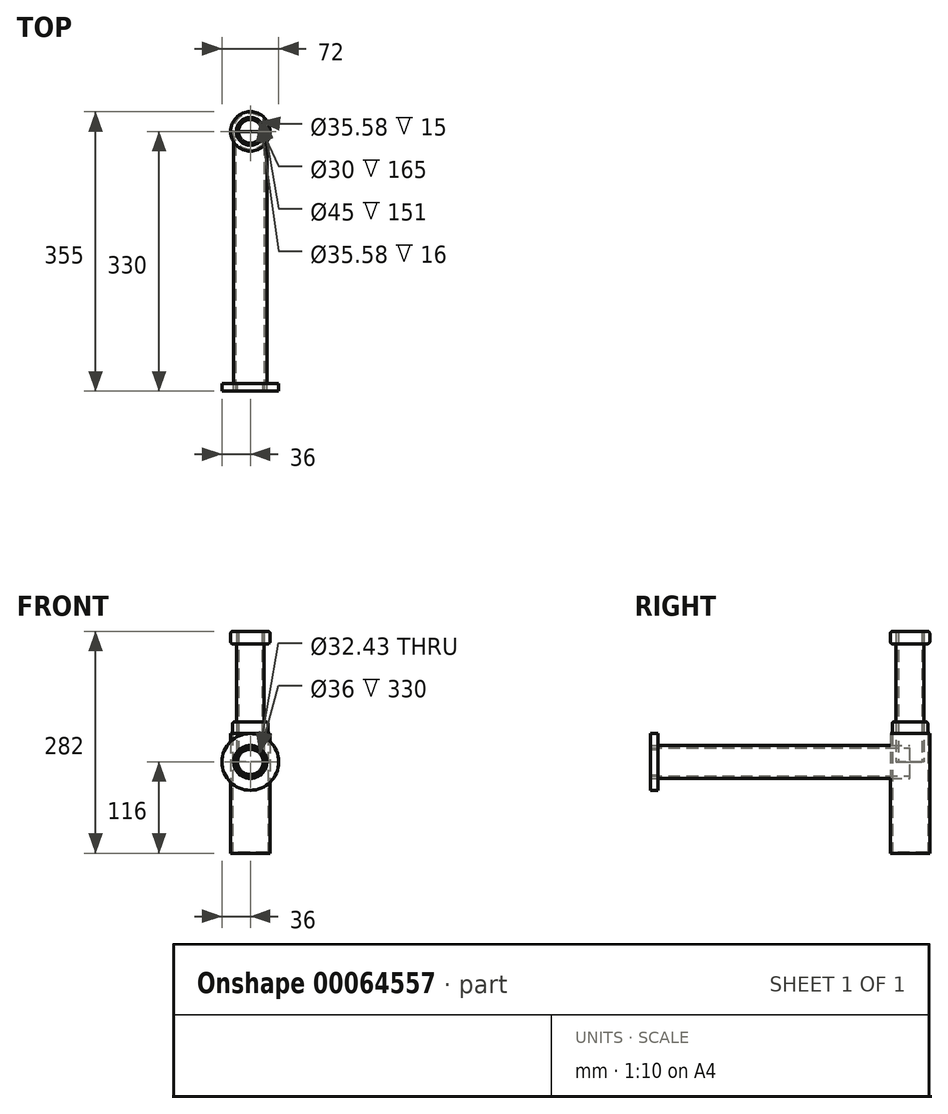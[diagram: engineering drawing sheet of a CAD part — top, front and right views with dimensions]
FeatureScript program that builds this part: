
annotation { "Feature Type Name" : "Feature", "Feature Type Description" : "" }
export const myFeature = defineFeature(function(context is Context, id is Id, definition is map)
    precondition{}
    {
        {
            var Q0;
            Q0=qCreatedBy(makeId("Front.planeOp"),FACE);
            var sketch = newSketch(context, id + "F0", { "sketchPlane" : qUnion([Q0])});
            skCircle(sketch, "E0", {"center": v(0, 0) * mm, "radius": 21 * mm});
            skCircle(sketch, "E1", {"center": v(0, 0) * mm, "radius": 18 * mm});
            skSolve(sketch);
        }
        {
            var Q0;
            Q0=makeQuery(id+"F0.imprint","IMPRINT",FACE,{"disambiguationData":[TD([[makeQuery(id+"F0.imprint","IMPRINT",EDGE,{"derivedFrom":sQuery(id+"F0.wireOp",EDGE,"E0")}),1.0]])]});
            extrude(context, id + "F1", {"entities" : qUnion([Q0]), "depth" : 330 * mm});
        }
        {
            var Q0;
            Q0=qCreatedBy(makeId("Top.planeOp"),FACE);
            var sketch = newSketch(context, id + "F2", { "sketchPlane" : qUnion([Q0])});
            skCircle(sketch, "E2", {"center": v(0, 0) * mm, "radius": 25 * mm});
            skCircle(sketch, "E3", {"center": v(0, 0) * mm, "radius": 22.5 * mm});
            skSolve(sketch);
        }
        {
            var Q0;
            Q0=makeQuery(id+"F2.imprint","IMPRINT",FACE,{"disambiguationData":[TD([[makeQuery(id+"F2.imprint","IMPRINT",EDGE,{"derivedFrom":sQuery(id+"F2.wireOp",EDGE,"E2")}),1.0]])]});
            extrude(context, id + "F3", {"entities" : qUnion([Q0]), "depth" : 36 * mm, "hasSecondDirection" : true, "secondDirectionOppositeDirection" : true, "secondDirectionDepth" : 115 * mm});
        }
        {
            var Q0;
            Q0=makeQuery(id+"F3.opExtrude","CAP_FACE",FACE,{"disambiguationData":[OSD([sQuery(id+"F2.wireOp",EDGE,"E2"),sQuery(id+"F2.wireOp",EDGE,"E3")])],"isStart":false});
            var sketch = newSketch(context, id + "F4", { "sketchPlane" : qUnion([Q0])});
            skCircle(sketch, "E4", {"center": v(0, 0) * mm, "radius": 25 * mm});
            skCircle(sketch, "E5", {"center": v(0, 0) * mm, "radius": 17.79 * mm});
            skSolve(sketch);
        }
        {
            var Q0;
            Q0=makeQuery(id+"F4.imprint","IMPRINT",FACE,{"disambiguationData":[TD([[makeQuery(id+"F4.imprint","IMPRINT",EDGE,{"derivedFrom":sQuery(id+"F4.wireOp",EDGE,"E5")}),-1.0]])]});
            extrude(context, id + "F5", {"entities" : qUnion([Q0]), "depth" : 15 * mm});
        }
        {
            var Q0;
            Q0=makeQuery(id+"F5.opExtrude","CAP_EDGE",EDGE,{"disambiguationData":[OSD([sQuery(id+"F2.wireOp",EDGE,"E3")])],"isStart":false});
            fillet(context, id + "F6", {"entities" : qUnion([Q0]), "radius" : 2.5 * mm, "tangentPropagation" : true, "allowEdgeOverflow" : false});
        }
        {
            var Q0;
            Q0=makeQuery(id+"F3.opExtrude","CAP_FACE",FACE,{"disambiguationData":[OSD([sQuery(id+"F2.wireOp",EDGE,"E2"),sQuery(id+"F2.wireOp",EDGE,"E3")])],"isStart":true});
            var sketch = newSketch(context, id + "F7", { "sketchPlane" : qUnion([Q0])});
            skCircle(sketch, "E6", {"center": v(0, 0) * mm, "radius": 25 * mm});
            skSolve(sketch);
        }
        {
            var Q0;
            Q0 = qSketchRegion(id + "F7", true);
            extrude(context, id + "F8", {"entities" : qUnion([Q0]), "operationType" : NewBodyOperationType.ADD, "depth" : 1 * mm});
        }
        {
            var Q0;
            Q0=qCreatedBy(makeId("Top.planeOp"),FACE);
            var sketch = newSketch(context, id + "F9", { "sketchPlane" : qUnion([Q0])});
            skCircle(sketch, "E7", {"center": v(0, 0) * mm, "radius": 17.72 * mm});
            skCircle(sketch, "E8", {"center": v(0, 0) * mm, "radius": 15 * mm});
            skSolve(sketch);
        }
        {
            var Q0;
            Q0 = qSketchRegion(id + "F9", true);
            extrude(context, id + "F10", {"entities" : qUnion([Q0]), "depth" : 165 * mm});
        }
        {
            var Q0;
            Q0=makeQuery(id+"F10.opExtrude","CAP_FACE",FACE,{"disambiguationData":[OSD([sQuery(id+"F9.wireOp",EDGE,"E7"),sQuery(id+"F9.wireOp",EDGE,"E8")])],"isStart":false});
            var sketch = newSketch(context, id + "F11", { "sketchPlane" : qUnion([Q0])});
            skCircle(sketch, "E9", {"center": v(0, 0) * mm, "radius": 17.79 * mm});
            skCircle(sketch, "E10", {"center": v(0, 0) * mm, "radius": 25 * mm});
            skSolve(sketch);
        }
        {
            var Q0;
            Q0=makeQuery(id+"F11.imprint","IMPRINT",FACE,{"disambiguationData":[TD([[makeQuery(id+"F11.imprint","IMPRINT",EDGE,{"derivedFrom":sQuery(id+"F11.wireOp",EDGE,"E9")}),-1.0]])]});
            extrude(context, id + "F12", {"entities" : qUnion([Q0]), "depth" : 1 * mm, "hasSecondDirection" : true, "secondDirectionOppositeDirection" : true, "secondDirectionDepth" : 15 * mm});
        }
        {
            var Q0;
            Q0=makeQuery(id+"F12.opExtrude","CAP_EDGE",EDGE,{"disambiguationData":[OSD([sQuery(id+"F11.wireOp",EDGE,"E10")])],"isStart":false});
            var Q1;
            Q1=makeQuery(id+"F12.opExtrude","CAP_EDGE",EDGE,{"disambiguationData":[OSD([sQuery(id+"F11.wireOp",EDGE,"E10")])],"isStart":true});
            fillet(context, id + "F13", {"entities" : qUnion([Q0, Q1]), "radius" : 3 * mm, "tangentPropagation" : true, "allowEdgeOverflow" : false});
        }
        {
            var Q0;
            Q0=makeQuery(id+"F1.opExtrude","CAP_FACE",FACE,{"disambiguationData":[OSD([sQuery(id+"F0.wireOp",EDGE,"E0"),sQuery(id+"F0.wireOp",EDGE,"E1")])],"isStart":false});
            cPlane(context, id + "F14", {"entities" : qUnion([Q0]), "cplaneType" : CPlaneType.OFFSET, "offset" : 10 * mm, "oppositeDirection" : true, "width" : 150 * mm, "height" : 150 * mm});
        }
        {
            var Q0;
            Q0=qCreatedBy(id+"F14.planeOp",FACE);
            var sketch = newSketch(context, id + "F15", { "sketchPlane" : qUnion([Q0])});
            skCircle(sketch, "E11", {"center": v(0, 0) * mm, "radius": 36 * mm});
            skCircle(sketch, "E12", {"center": v(0, 0) * mm, "radius": 16.22 * mm});
            skSolve(sketch);
        }
        {
            var Q0;
            Q0 = qSketchRegion(id + "F15", true);
            extrude(context, id + "F16", {"entities" : qUnion([Q0]), "depth" : 10 * mm});
        }
    });
